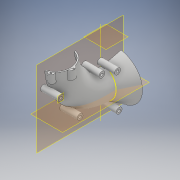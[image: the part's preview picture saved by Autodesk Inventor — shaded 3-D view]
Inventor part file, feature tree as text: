
AUTODESK INVENTOR PART (.ipt)
format: ipt  version: 2017 (Build 210142000, 142)  size: 399,872 bytes
history: native  units: mm
features: sketch x10, projected_geometry x6, other x4, extrude x3, sweep x1, loft x1
ambient origin geometry x8: Origin, YZ Plane, XZ Plane, XY Plane, X Axis, Y Axis, Z Axis, Center Point
bodies: Body1 (feature_tree)
feature tree (25):
  sketch  "Esquisse1"
  sketch  "Esquisse2"
  other  "Plan de construction1"
  sketch  "Esquisse3"
  sketch  "Esquisse4"
  other  "Plan de construction2"
  sketch  "Esquisse6"
  sweep  "Balayage2"
  sketch  "Esquisse8"
  loft  "Lissage2"
  extrude  "Extrusion1"  Depth=54.0mm
  other  "Plan de construction3"
  extrude  "Extrusion3"  Depth=70.0mm
  extrude  "Extrusion4"  Depth=75.0mm
  sketch  "Esquisse7"
  projected_geometry  "Boucle projetée1"
  other  "Arêtes1"
  sketch  "Esquisse9"
  projected_geometry  "Boucle projetée2"
  projected_geometry  "Boucle projetée3"
  projected_geometry  "Boucle projetée4"
  projected_geometry  "Boucle projetée5"
  sketch  "Esquisse10"
  sketch  "Esquisse11"
  projected_geometry  "Boucle projetée6"
